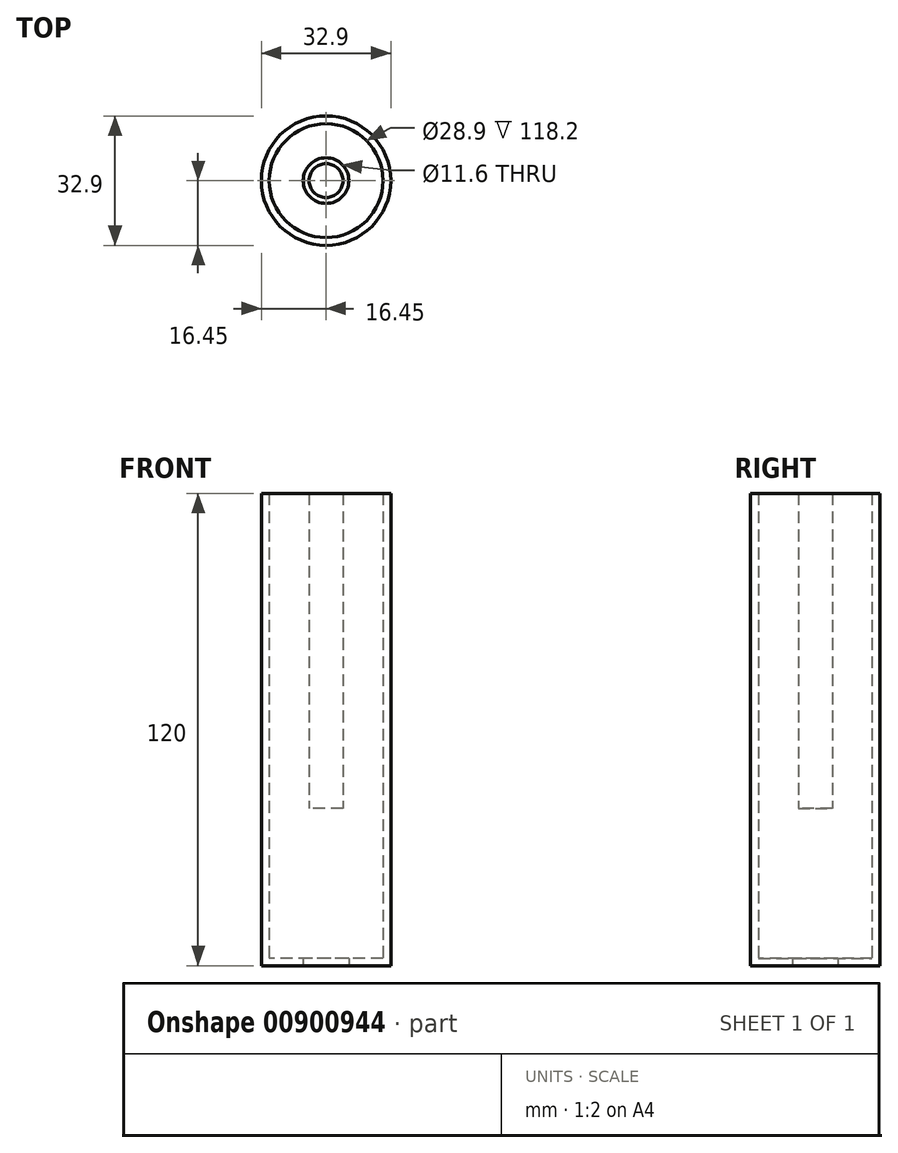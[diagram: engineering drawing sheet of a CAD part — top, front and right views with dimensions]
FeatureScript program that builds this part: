
annotation { "Feature Type Name" : "Feature", "Feature Type Description" : "" }
export const myFeature = defineFeature(function(context is Context, id is Id, definition is map)
    precondition{}
    {
        {
            var Q0;
            Q0=qCreatedBy(makeId("Top.planeOp"),FACE);
            var sketch = newSketch(context, id + "F0", { "sketchPlane" : qUnion([Q0])});
            skCircle(sketch, "E0", {"center": v(0, 0) * mm, "radius": 4.3 * mm});
            skCircle(sketch, "E1", {"center": v(0, 0) * mm, "radius": 14.45 * mm});
            skCircle(sketch, "E2", {"center": v(0, 0) * mm, "radius": 16.45 * mm});
            skCircle(sketch, "E3", {"center": v(0, 0) * mm, "radius": 5.8 * mm});
            skSolve(sketch);
        }
        {
            var Q0;
            Q0 = qSketchRegion(id + "F0", true);
            extrude(context, id + "F1", {"entities" : qUnion([Q0]), "depth" : 120 * mm, "offsetDistance" : 25 * mm});
        }
        {
            var Q0;
            Q0=makeQuery(id+"F0.imprint","IMPRINT",FACE,{"disambiguationData":[TD([[makeQuery(id+"F0.imprint","IMPRINT",EDGE,{"derivedFrom":sQuery(id+"F0.wireOp",EDGE,"E1")}),1.0]])]});
            extrude(context, id + "F2", {"entities" : qUnion([Q0]), "operationType" : NewBodyOperationType.ADD, "depth" : 1.8 * mm, "offsetDistance" : 25 * mm});
        }
        {
            var Q0;
            Q0=makeQuery(id+"F0.imprint","IMPRINT",FACE,{"disambiguationData":[TD([[makeQuery(id+"F0.imprint","IMPRINT",EDGE,{"derivedFrom":sQuery(id+"F0.wireOp",EDGE,"E0")}),1.0]])]});
            extrude(context, id + "F3", {"entities" : qUnion([Q0]), "depth" : 120 * mm, "offsetDistance" : 25 * mm, "hasSecondDirection" : true, "secondDirectionOppositeDirection" : false, "secondDirectionDepth" : 40 * mm});
        }
    });
